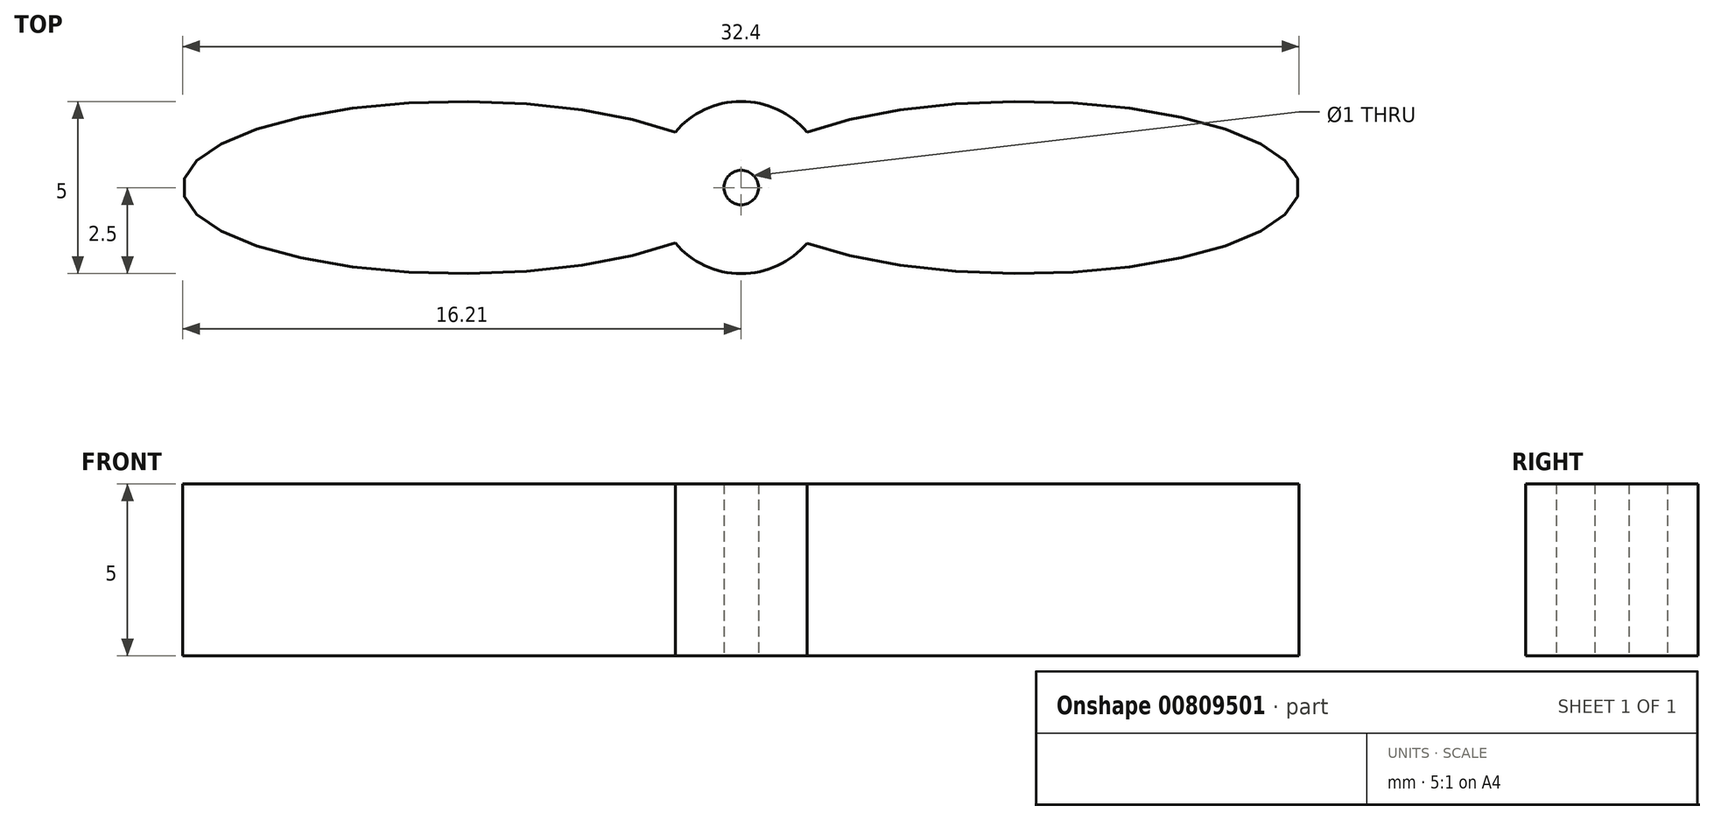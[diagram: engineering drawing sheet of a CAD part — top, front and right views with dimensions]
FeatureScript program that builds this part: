
annotation { "Feature Type Name" : "Feature", "Feature Type Description" : "" }
export const myFeature = defineFeature(function(context is Context, id is Id, definition is map)
    precondition{}
    {
        {
            var Q0;
            Q0=qCreatedBy(makeId("Top.planeOp"),FACE);
            var sketch = newSketch(context, id + "F0", { "sketchPlane" : qUnion([Q0])});
            skEllipticalArc(sketch, "E0", {});
            skEllipticalArc(sketch, "E1.MirrorC", {});
            skCircle(sketch, "E2", {"center": v(0, 0) * mm, "radius": 2.5 * mm});
            skCircle(sketch, "E3", {"center": v(0, 0) * mm, "radius": 0.5 * mm});
            const initialGuessF0  = {"E0": [0.00809546628454171, 0, 1, 0, 0.00809546628454171, 0.0025, 3.8428214069128197, 2.440363900266765], "E1.MirrorC": [-0.00810973532497883, 0, 1, 0, 0.00809546628454171, 0.0025, 0.6991387479479004, 5.58404655923187]};
            skSetInitialGuess(sketch, initialGuessF0);
            skSolve(sketch);
        }
        {
            var Q0;
            Q0 = qSketchRegion(id + "F0", true);
            extrude(context, id + "F1", {"entities" : qUnion([Q0]), "depth" : 5 * mm, "offsetDistance" : 25.4 * mm});
        }
    });
